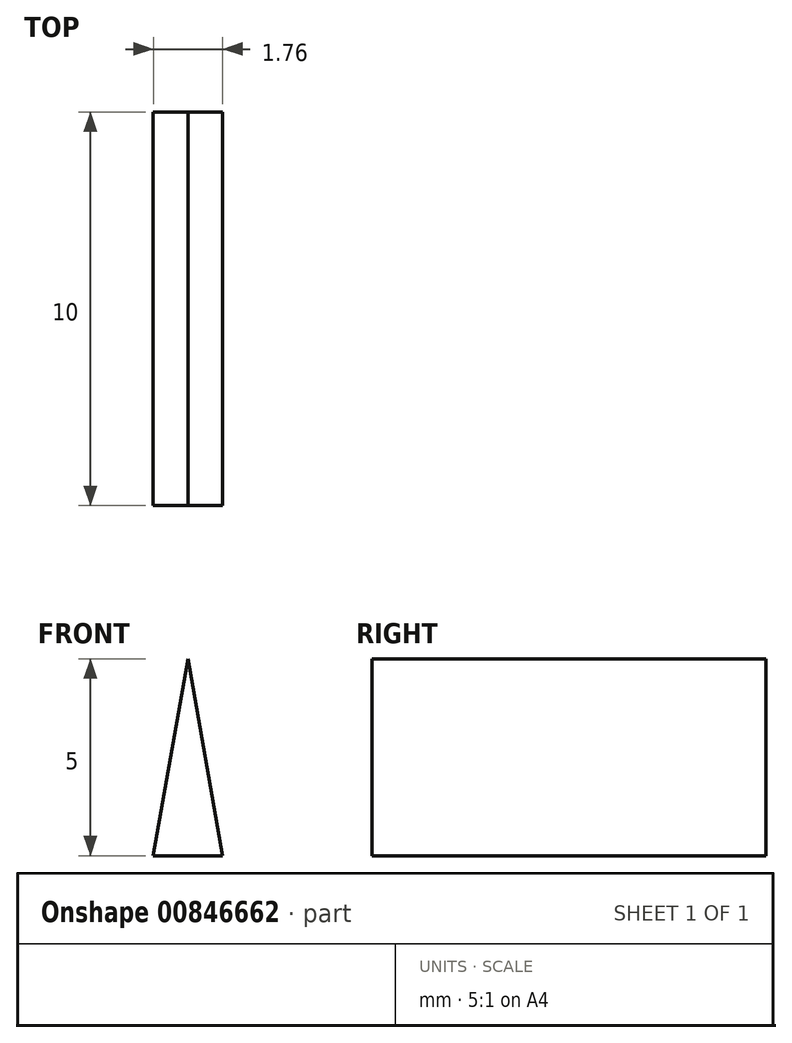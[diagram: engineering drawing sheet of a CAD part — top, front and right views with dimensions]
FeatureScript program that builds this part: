
annotation { "Feature Type Name" : "Feature", "Feature Type Description" : "" }
export const myFeature = defineFeature(function(context is Context, id is Id, definition is map)
    precondition{}
    {
        {
            var Q0;
            Q0=qCreatedBy(makeId("Front.planeOp"),FACE);
            var sketch = newSketch(context, id + "F0", { "sketchPlane" : qUnion([Q0])});
            skLineSegment(sketch, "E0", {"start": v(0, 5) * mm, "end": v(0.88, 0) * mm});
            skLineSegment(sketch, "E1", {"start": v(0.88, 0) * mm, "end": v(-0.88, 0) * mm});
            skLineSegment(sketch, "E2", {"start": v(-0.88, 0) * mm, "end": v(0, 5) * mm});
            skSolve(sketch);
        }
        {
            var Q0;
            Q0 = qSketchRegion(id + "F0", true);
            extrude(context, id + "F1", {"entities" : qUnion([Q0]), "depth" : 10 * mm, "offsetDistance" : 25 * mm});
        }
    });
